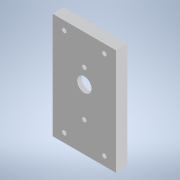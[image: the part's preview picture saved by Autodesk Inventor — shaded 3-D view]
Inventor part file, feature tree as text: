
AUTODESK INVENTOR PART (.ipt)
format: ipt  version: 2021 (Build 250183000, 183)  size: 180,224 bytes
history: native  units: in
note: dims shown in document units (in); Inventor stores cm internally (conversion verified against a paired STEP export)
features: extrude x7, sketch x4
ambient origin geometry x8: Origin, YZ Plane, XZ Plane, XY Plane, X Axis, Y Axis, Z Axis, Center Point
bodies: Solid1 (feature_tree)
feature tree (11):
  sketch  "Sketch1"  dims[d0=0.1142in d1=0.1142in]
  extrude  "Extrusion1"  Depth=0.1142in
  sketch  "Sketch2"  dims[d2=0.1142in d3=0.1142in]
  extrude  "Extrusion2"  Depth=0.1142in
  extrude  "Extrusion3"  Depth=0.1181in
  extrude  "Extrusion4"  Depth=0.0394in
  sketch  "Sketch3"  dims[d4=0.1181in d5=0.0in d6=0.0197in]
  extrude  "Extrusion5"  Depth=0.0787in
  extrude  "Extrusion6"  Depth=0.0394in
  extrude  "Extrusion7"  Depth=0.0787in
  sketch  "Sketch4"  dims[d7=0.0787in d8=0.0197in d9=0.0787in d10=0.0197in d11=0.0787in d12=0.0197in d13=0.0787in d14=0.0787in d15=0.0in d16=0.1181in d17=0.0in d18=0.1772in d19=0.0in d20=0.1142in d21=0.2362in d22=1.1811in d23=0.1142in d24=0.2362in d25=0.3937in d26=0.0in d27=0.0394in d28=0.0in d30=0.3754in d31=0.0in d32=0.0in]
